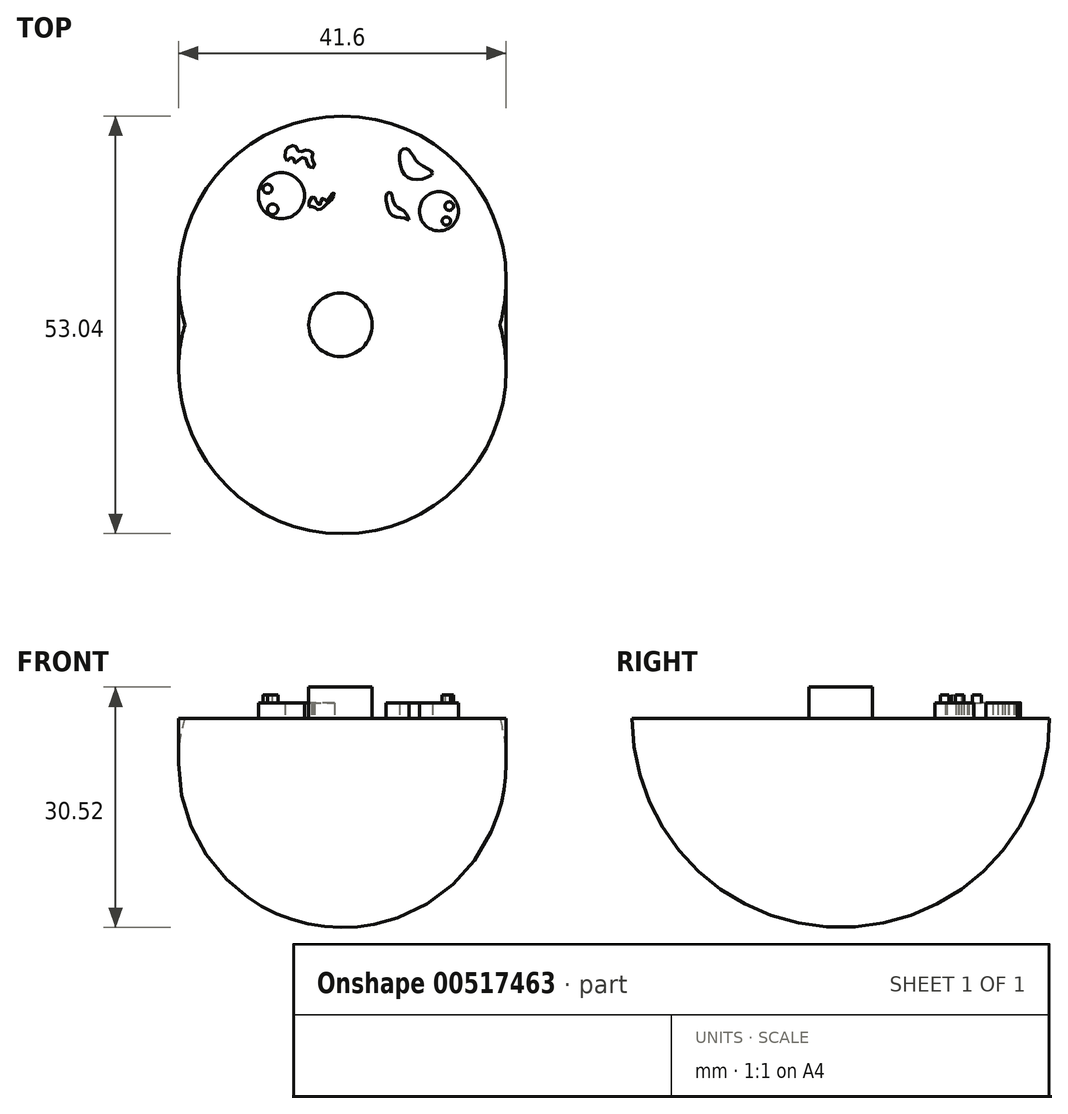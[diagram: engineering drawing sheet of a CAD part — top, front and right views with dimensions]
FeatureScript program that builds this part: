
annotation { "Feature Type Name" : "Feature", "Feature Type Description" : "" }
export const myFeature = defineFeature(function(context is Context, id is Id, definition is map)
    precondition{}
    {
        {
            var Q0;
            Q0=qCreatedBy(makeId("Top.planeOp"),FACE);
            var sketch = newSketch(context, id + "F0", { "sketchPlane" : qUnion([Q0])});
            skLineSegment(sketch, "E0", {"start": v(0, 0) * mm, "end": v(-40, 0) * mm});
            skArc(sketch, "E1", {"start": v(0, 0) * mm, "mid": v(-20, 26.52) * mm, "end": v(-40, 0) * mm});
            skSolve(sketch);
        }
        {
            var Q0;
            Q0=makeQuery(id+"F0.imprint","IMPRINT",FACE,{"disambiguationData":[TD([[makeQuery(id+"F0.imprint","IMPRINT",EDGE,{"derivedFrom":sQuery(id+"F0.wireOp",EDGE,"E0")}),-1.0]])]});
            var Q1;
            Q1=sQuery(id+"F0.wireOp",EDGE,"E0");
            revolve(context, id + "F1", {"entities" : qUnion([Q0]), "axis" : qUnion([Q1]), "revolveType" : RevolveType.ONE_DIRECTION, "angle" : 180 * degree});
        }
        {
            var Q0;
            Q0=qCreatedBy(makeId("Top.planeOp"),FACE);
            var sketch = newSketch(context, id + "F2", { "sketchPlane" : qUnion([Q0])});
            skCircle(sketch, "E2", {"center": v(-20.24, 0) * mm, "radius": 4.03 * mm});
            skSolve(sketch);
        }
        {
            var Q0;
            Q0=makeQuery(id+"F2.imprint","IMPRINT",FACE,{"disambiguationData":[TD([[makeQuery(id+"F2.imprint","IMPRINT",EDGE,{"derivedFrom":sQuery(id+"F2.wireOp",EDGE,"E2")}),1.0]])]});
            extrude(context, id + "F3", {"entities" : qUnion([Q0]), "operationType" : NewBodyOperationType.ADD, "depth" : 4 * mm, "offsetDistance" : 25 * mm});
        }
        {
            var Q0;
            Q0=makeQuery(id+"F3.opExtrude","CAP_FACE",FACE,{"disambiguationData":[OSD([sQuery(id+"F2.wireOp",EDGE,"E2")])],"isStart":false});
            var sketch = newSketch(context, id + "F4", { "sketchPlane" : qUnion([Q0])});
            skSolve(sketch);
        }
        {
            var Q0;
            Q0=makeQuery(id+"F4.imprint","IMPRINT",FACE,{"disambiguationData":[TD([[makeQuery(id+"F4.imprint","IMPRINT",EDGE,{"derivedFrom":makeQuery(id+"F3.opExtrude","CAP_EDGE",EDGE,{"disambiguationData":[OSD([sQuery(id+"F2.wireOp",EDGE,"E2")])],"isStart":false})}),1.0]])]});
            var sketch = newSketch(context, id + "F5", { "sketchPlane" : qUnion([Q0])});
            skFitSpline(sketch, "E3", {"points": [v(-23.2, 1.7) * mm, v(-23.67, 1.05) * mm, v(-23.83, 0) * mm, v(-23.75, -0.95) * mm, v(-23.6, -1.62) * mm, v(-22.96, -2.33) * mm, v(-22.1, -2.77) * mm, v(-21.41, -2.27) * mm, v(-22.28, -1.09) * mm, v(-23.08, -1.09) * mm, v(-23.4, 0) * mm, v(-23.03, 0.8) * mm, v(-22.46, 1.56) * mm, v(-22.48, 2.55) * mm, v(-22, 3.2) * mm, v(-20.66, 1.94) * mm, v(-21.58, 1.6) * mm, v(-21.7, 0) * mm, v(-20.41, -1.42) * mm, v(-20.36, -2.98) * mm, v(-19.5, -2.95) * mm, v(-18.28, -2.32) * mm, v(-18.03, -1.36) * mm, v(-18.88, -0.8) * mm, v(-19.55, -1.47) * mm, v(-19.95, 0) * mm, v(-20.43, 0.99) * mm, v(-19.7, 1.68) * mm, v(-19.99, 2.79) * mm, v(-19.59, 3.56) * mm, v(-17.66, 2.15) * mm, v(-18.5, 1.05) * mm, v(-18.73, 0) * mm, v(-17.17, 0) * mm, v(-16.82, -1.34) * mm], "startDerivative": vector(-21.2, -24.03) * mm, "endDerivative": vector(-1.42, -55.14) * mm});
            skSolve(sketch);
        }
        {
            var Q0;
            Q0=sQuery(id+"F5.wireOp",EDGE,"E3");
            extrude(context, id + "F6", {"bodyType" : ToolBodyType.SURFACE, "surfaceEntities" : qUnion([Q0]), "depth" : 1 * mm, "offsetDistance" : 25 * mm});
        }
        {
            var Q0;
            Q0=makeQuery(id+"F1.opRevolve","CAP_FACE",FACE,{"disambiguationData":[OSD([sQuery(id+"F0.wireOp",EDGE,"E0"),sQuery(id+"F0.wireOp",EDGE,"E1")])],"isStart":false});
            var sketch = newSketch(context, id + "F7", { "sketchPlane" : qUnion([Q0])});
            skCircle(sketch, "E4", {"center": v(-7.72, 14.44) * mm, "radius": 2.49 * mm});
            skSolve(sketch);
        }
        {
            var Q0;
            Q0 = qSketchRegion(id + "F7", true);
            extrude(context, id + "F8", {"entities" : qUnion([Q0]), "operationType" : NewBodyOperationType.ADD, "depth" : 2 * mm, "offsetDistance" : 25 * mm});
        }
        {
            var Q0;
            Q0=makeQuery(id+"F1.opRevolve","CAP_FACE",FACE,{"disambiguationData":[OSD([sQuery(id+"F0.wireOp",EDGE,"E0"),sQuery(id+"F0.wireOp",EDGE,"E1")])],"isStart":false});
            var sketch = newSketch(context, id + "F9", { "sketchPlane" : qUnion([Q0])});
            skCircle(sketch, "E5", {"center": v(-27.74, 16.41) * mm, "radius": 2.93 * mm});
            skSolve(sketch);
        }
        {
            var Q0;
            Q0 = qSketchRegion(id + "F9", true);
            extrude(context, id + "F10", {"entities" : qUnion([Q0]), "operationType" : NewBodyOperationType.ADD, "depth" : 2 * mm, "offsetDistance" : 25 * mm});
        }
        {
            var Q0;
            Q0=makeQuery(id+"F8.opExtrude","CAP_FACE",FACE,{"disambiguationData":[OSD([sQuery(id+"F7.wireOp",EDGE,"E4")])],"isStart":false});
            var sketch = newSketch(context, id + "F11", { "sketchPlane" : qUnion([Q0])});
            skSolve(sketch);
        }
        {
            var Q0;
            Q0=makeQuery(id+"F11.imprint","IMPRINT",FACE,{"disambiguationData":[TD([[makeQuery(id+"F11.imprint","IMPRINT",EDGE,{"derivedFrom":makeQuery(id+"F8.opExtrude","CAP_EDGE",EDGE,{"disambiguationData":[OSD([sQuery(id+"F7.wireOp",EDGE,"E4")])],"isStart":false})}),1.0]])]});
            var sketch = newSketch(context, id + "F12", { "sketchPlane" : qUnion([Q0])});
            skCircle(sketch, "E6", {"center": v(-6.8, 13.19) * mm, "radius": 0.53 * mm});
            skSolve(sketch);
        }
        {
            var Q0;
            Q0 = qSketchRegion(id + "F12", true);
            extrude(context, id + "F13", {"entities" : qUnion([Q0]), "operationType" : NewBodyOperationType.ADD, "depth" : 1 * mm, "offsetDistance" : 25 * mm});
        }
        {
            var Q0;
            Q0=makeQuery(id+"F11.imprint","IMPRINT",FACE,{"disambiguationData":[TD([[makeQuery(id+"F11.imprint","IMPRINT",EDGE,{"derivedFrom":makeQuery(id+"F8.opExtrude","CAP_EDGE",EDGE,{"disambiguationData":[OSD([sQuery(id+"F7.wireOp",EDGE,"E4")])],"isStart":false})}),1.0]])]});
            var sketch = newSketch(context, id + "F14", { "sketchPlane" : qUnion([Q0])});
            skCircle(sketch, "E7", {"center": v(-6.42, 15.1) * mm, "radius": 0.54 * mm});
            skSolve(sketch);
        }
        {
            var Q0;
            Q0 = qSketchRegion(id + "F14", true);
            extrude(context, id + "F15", {"entities" : qUnion([Q0]), "operationType" : NewBodyOperationType.ADD, "depth" : 1 * mm, "offsetDistance" : 25 * mm});
        }
        {
            var Q0;
            Q0=makeQuery(id+"F10.opExtrude","CAP_FACE",FACE,{"disambiguationData":[OSD([sQuery(id+"F9.wireOp",EDGE,"E5")])],"isStart":false});
            var sketch = newSketch(context, id + "F16", { "sketchPlane" : qUnion([Q0])});
            skSolve(sketch);
        }
        {
            var Q0;
            Q0=makeQuery(id+"F16.imprint","IMPRINT",FACE,{"disambiguationData":[TD([[makeQuery(id+"F16.imprint","IMPRINT",EDGE,{"derivedFrom":makeQuery(id+"F10.opExtrude","CAP_EDGE",EDGE,{"disambiguationData":[OSD([sQuery(id+"F9.wireOp",EDGE,"E5")])],"isStart":false})}),1.0]])]});
            var sketch = newSketch(context, id + "F17", { "sketchPlane" : qUnion([Q0])});
            skCircle(sketch, "E8", {"center": v(-28.85, 14.7) * mm, "radius": 0.66 * mm});
            skSolve(sketch);
        }
        {
            var Q0;
            Q0=makeQuery(id+"F17.imprint","IMPRINT",FACE,{"disambiguationData":[TD([[makeQuery(id+"F17.imprint","IMPRINT",EDGE,{"derivedFrom":sQuery(id+"F17.wireOp",EDGE,"E8")}),1.0]])]});
            extrude(context, id + "F18", {"entities" : qUnion([Q0]), "operationType" : NewBodyOperationType.ADD, "depth" : 1 * mm, "offsetDistance" : 25 * mm});
        }
        {
            var Q0;
            Q0=makeQuery(id+"F16.imprint","IMPRINT",FACE,{"disambiguationData":[TD([[makeQuery(id+"F16.imprint","IMPRINT",EDGE,{"derivedFrom":makeQuery(id+"F10.opExtrude","CAP_EDGE",EDGE,{"disambiguationData":[OSD([sQuery(id+"F9.wireOp",EDGE,"E5")])],"isStart":false})}),1.0]])]});
            var sketch = newSketch(context, id + "F19", { "sketchPlane" : qUnion([Q0])});
            skCircle(sketch, "E9", {"center": v(-29.5, 17.29) * mm, "radius": 0.57 * mm});
            skSolve(sketch);
        }
        {
            var Q0;
            Q0 = qSketchRegion(id + "F19", true);
            extrude(context, id + "F20", {"entities" : qUnion([Q0]), "operationType" : NewBodyOperationType.ADD, "depth" : 1 * mm, "offsetDistance" : 25 * mm});
        }
        {
            var Q0;
            Q0=makeQuery(id+"F1.opRevolve","CAP_FACE",FACE,{"disambiguationData":[OSD([sQuery(id+"F0.wireOp",EDGE,"E0"),sQuery(id+"F0.wireOp",EDGE,"E1")])],"isStart":false});
            var sketch = newSketch(context, id + "F21", { "sketchPlane" : qUnion([Q0])});
            skFitSpline(sketch, "E10", {"points": [v(-8.52, 19.31) * mm, v(-10.28, 20.5) * mm, v(-11.5, 22.14) * mm, v(-12.47, 22.25) * mm, v(-12.44, 19.67) * mm, v(-10.54, 18.46) * mm, v(-8.52, 19.31) * mm]});
            skSolve(sketch);
        }
        {
            var Q0;
            Q0 = qSketchRegion(id + "F21", true);
            extrude(context, id + "F22", {"entities" : qUnion([Q0]), "operationType" : NewBodyOperationType.ADD, "depth" : 2 * mm, "offsetDistance" : 25 * mm});
        }
        {
            var Q0;
            Q0=makeQuery(id+"F1.opRevolve","CAP_FACE",FACE,{"disambiguationData":[OSD([sQuery(id+"F0.wireOp",EDGE,"E0"),sQuery(id+"F0.wireOp",EDGE,"E1")])],"isStart":false});
            var sketch = newSketch(context, id + "F23", { "sketchPlane" : qUnion([Q0])});
            skFitSpline(sketch, "E11", {"points": [v(-11.5, 13.3) * mm, v(-12.16, 14.45) * mm, v(-13.04, 14.96) * mm, v(-13.65, 16.06) * mm, v(-13.83, 16.8) * mm, v(-14.35, 16.66) * mm, v(-14.38, 15.5) * mm, v(-13.61, 13.87) * mm, v(-12.06, 13.56) * mm, v(-11.5, 13.3) * mm]});
            skSolve(sketch);
        }
        {
            var Q0;
            Q0 = qSketchRegion(id + "F23", true);
            extrude(context, id + "F24", {"entities" : qUnion([Q0]), "operationType" : NewBodyOperationType.ADD, "depth" : 2 * mm, "offsetDistance" : 25 * mm});
        }
        {
            var Q0;
            Q0=makeQuery(id+"F1.opRevolve","CAP_FACE",FACE,{"disambiguationData":[OSD([sQuery(id+"F0.wireOp",EDGE,"E0"),sQuery(id+"F0.wireOp",EDGE,"E1")])],"isStart":false});
            var sketch = newSketch(context, id + "F25", { "sketchPlane" : qUnion([Q0])});
            skFitSpline(sketch, "E12", {"points": [v(-27, 20.84) * mm, v(-27.25, 21.98) * mm, v(-26.76, 22.59) * mm, v(-25.97, 22.76) * mm, v(-25.55, 22) * mm, v(-24.84, 22.16) * mm, v(-24.23, 22.13) * mm, v(-23.7, 21.68) * mm, v(-23.88, 21.1) * mm, v(-23.52, 20.45) * mm, v(-23.78, 19.93) * mm, v(-24.37, 20.33) * mm, v(-24.66, 21.15) * mm, v(-25.44, 21.12) * mm, v(-25.99, 20.56) * mm, v(-26.34, 21.33) * mm, v(-27, 20.84) * mm]});
            skSolve(sketch);
        }
        {
            var Q0;
            Q0 = qSketchRegion(id + "F25", true);
            extrude(context, id + "F26", {"entities" : qUnion([Q0]), "operationType" : NewBodyOperationType.ADD, "depth" : 2 * mm, "offsetDistance" : 25 * mm});
        }
        {
            var Q0;
            Q0=makeQuery(id+"F1.opRevolve","CAP_FACE",FACE,{"disambiguationData":[OSD([sQuery(id+"F0.wireOp",EDGE,"E0"),sQuery(id+"F0.wireOp",EDGE,"E1")])],"isStart":false});
            var sketch = newSketch(context, id + "F27", { "sketchPlane" : qUnion([Q0])});
            skFitSpline(sketch, "E13", {"points": [v(-24.23, 15.02) * mm, v(-23.65, 15) * mm, v(-23.22, 14.68) * mm, v(-22.71, 14.7) * mm, v(-22.26, 15.17) * mm, v(-21.72, 15.57) * mm, v(-21.25, 16.14) * mm, v(-21.03, 16.74) * mm, v(-21.7, 16.16) * mm, v(-21.98, 15.67) * mm, v(-22.37, 16.04) * mm, v(-22.7, 15.86) * mm, v(-22.82, 15.3) * mm, v(-23.3, 15.6) * mm, v(-23.44, 16.1) * mm, v(-23.84, 16.23) * mm, v(-24.23, 15.02) * mm]});
            skSolve(sketch);
        }
        {
            var Q0;
            Q0 = qSketchRegion(id + "F27", true);
            extrude(context, id + "F28", {"entities" : qUnion([Q0]), "operationType" : NewBodyOperationType.ADD, "depth" : 2 * mm, "offsetDistance" : 25 * mm});
        }
    });
